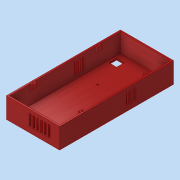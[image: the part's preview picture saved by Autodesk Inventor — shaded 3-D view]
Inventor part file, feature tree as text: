
AUTODESK INVENTOR PART (.ipt)
format: ipt  version: 2022 (Build 260153000, 153)  size: 285,184 bytes
history: native  units: in
note: dims shown in document units (in); Inventor stores cm internally (conversion verified against a paired STEP export)
features: extrude x8, sketch x8, chamfer x1
ambient origin geometry x8: Origin, YZ Plane, XZ Plane, XY Plane, X Axis, Y Axis, Z Axis, Center Point
bodies: Solid1 (feature_tree)
feature tree (17):
  extrude  "Extrusion1"  Depth=11.811in
  extrude  "Extrusion2"  Depth=0.1575in
  extrude  "Extrusion3"  Depth=0.1575in
  extrude  "Extrusion4"  Depth=1.9685in TaperAngle=0.0deg
  chamfer  "Chamfer1"  Distance=0.6299in
  extrude  "Extrusion5"  Depth=0.1969in
  extrude  "Extrusion6"  Depth=0.2362in TaperAngle=0.0deg
  extrude  "Extrusion7"  Depth=0.2362in TaperAngle=45.0deg
  extrude  "Extrusion8"  Depth=0.7874in
  sketch  "Sketch1"  dims[d0=5.5118in d1=11.811in]
  sketch  "Sketch2"  dims[d2=0.1575in d3=0.0in d4=0.1575in]
  sketch  "Sketch3"  dims[d5=0.1575in d6=0.1575in]
  sketch  "Sketch4"  dims[d7=0.1575in d8=1.9685in d9=0.0in]
  sketch  "Sketch5"  dims[d10=0.3937in]
  sketch  "Sketch6"  dims[d11=0.3937in]
  sketch  "Sketch7"  dims[d12=2.3622in d13=0.6299in d14=0.0in]
  sketch  "Sketch9"  dims[d15=0.1969in d16=0.1969in d17=0.2362in d18=0.0in d19=0.2362in d20=0.0787in d21=45.0deg d22=0.7874in d23=0.7874in d24=0.7874in d26=1.5748in d27=0.2362in d28=0.0in d29=4.5276in d30=8.4646in d31=1.9685in d32=5.9055in d33=1.2795in d34=0.1772in d35=0.1772in d36=0.1772in d37=0.1772in d38=0.3346in d39=0.3937in d40=0.0in d42=1.1811in d45=0.1969in d47=0.1969in d48=0.1969in d49=0.1969in d50=0.1969in d51=0.1969in d52=0.1969in d53=0.1969in d54=0.3937in d55=0.9843in d56=0.1969in d57=0.3937in d58=0.0in d60=1.1811in d61=0.1969in d62=0.1969in d63=0.1969in d64=1.1811in d65=0.3937in d66=5.5118in d67=0.0in d68=0.1969in d69=1.1811in d70=0.1969in d71=1.1811in d72=0.1969in d73=0.1969in d74=3.937in]
